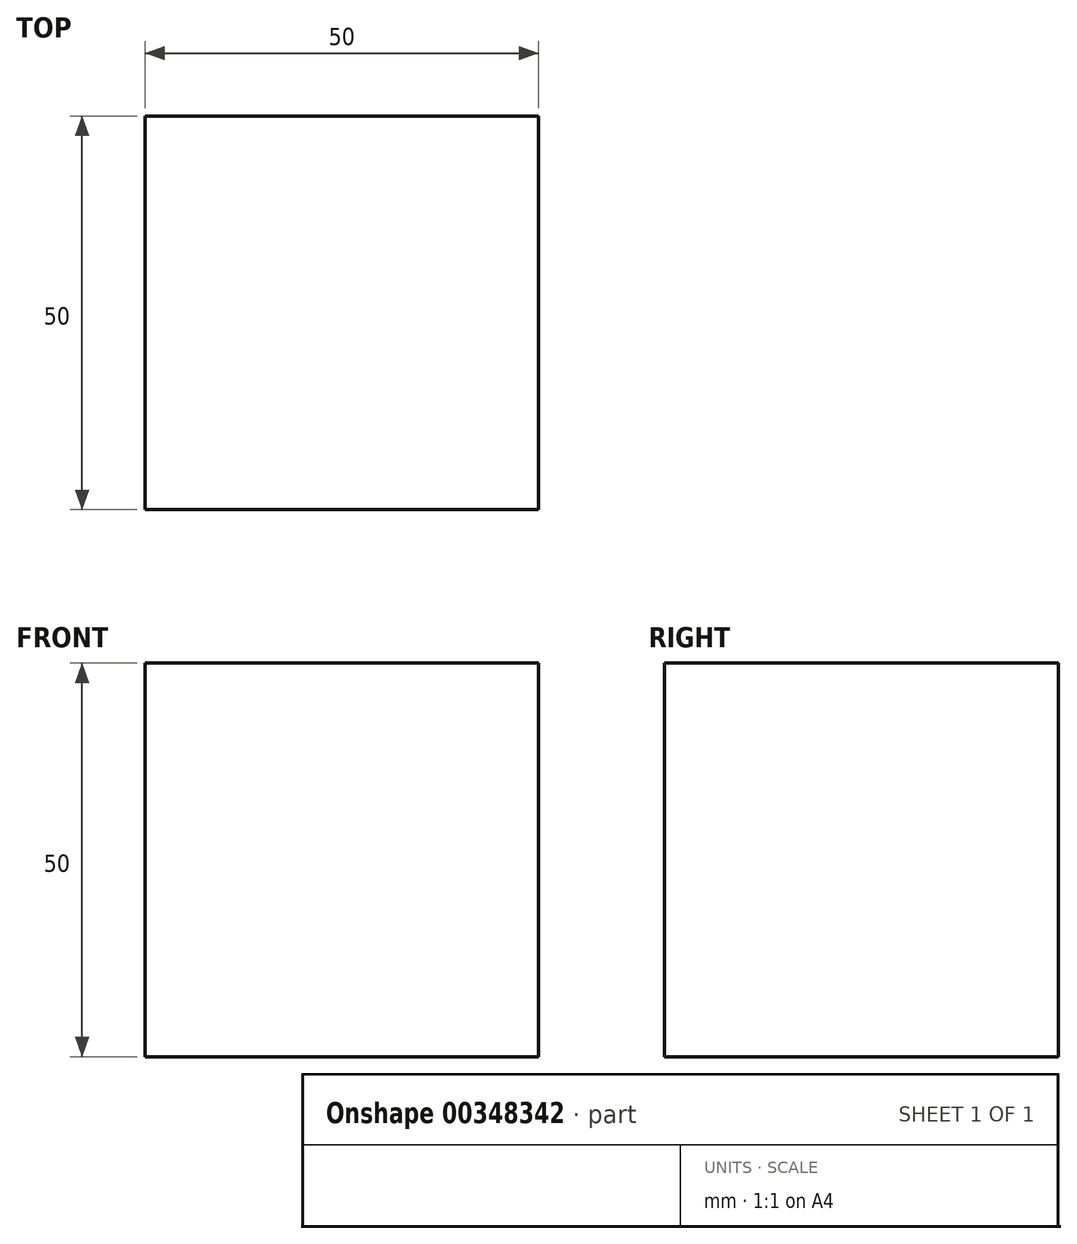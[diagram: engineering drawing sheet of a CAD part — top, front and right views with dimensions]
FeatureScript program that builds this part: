
annotation { "Feature Type Name" : "Feature", "Feature Type Description" : "" }
export const myFeature = defineFeature(function(context is Context, id is Id, definition is map)
    precondition{}
    {
        {
            var Q0;
            Q0=qCreatedBy(makeId("Front.planeOp"),FACE);
            var sketch = newSketch(context, id + "F0", { "sketchPlane" : qUnion([Q0])});
            skLineSegment(sketch, "E0.bottom", {"start": v(-50, 50) * mm, "end": v(0, 50) * mm});
            skLineSegment(sketch, "E0.top", {"start": v(-50, 0) * mm, "end": v(0, 0) * mm});
            skLineSegment(sketch, "E0.left", {"start": v(-50, 50) * mm, "end": v(-50, 0) * mm});
            skLineSegment(sketch, "E0.right", {"start": v(0, 50) * mm, "end": v(0, 0) * mm});
            skSolve(sketch);
        }
        {
            var Q0;
            Q0=makeQuery(id+"F0.imprint","IMPRINT",FACE,{"disambiguationData":[TD([[makeQuery(id+"F0.imprint","IMPRINT",EDGE,{"derivedFrom":sQuery(id+"F0.wireOp",EDGE,"E0.bottom")}),-1.0]])]});
            extrude(context, id + "F1", {"entities" : qUnion([Q0]), "depth" : 50 * mm});
        }
    });
